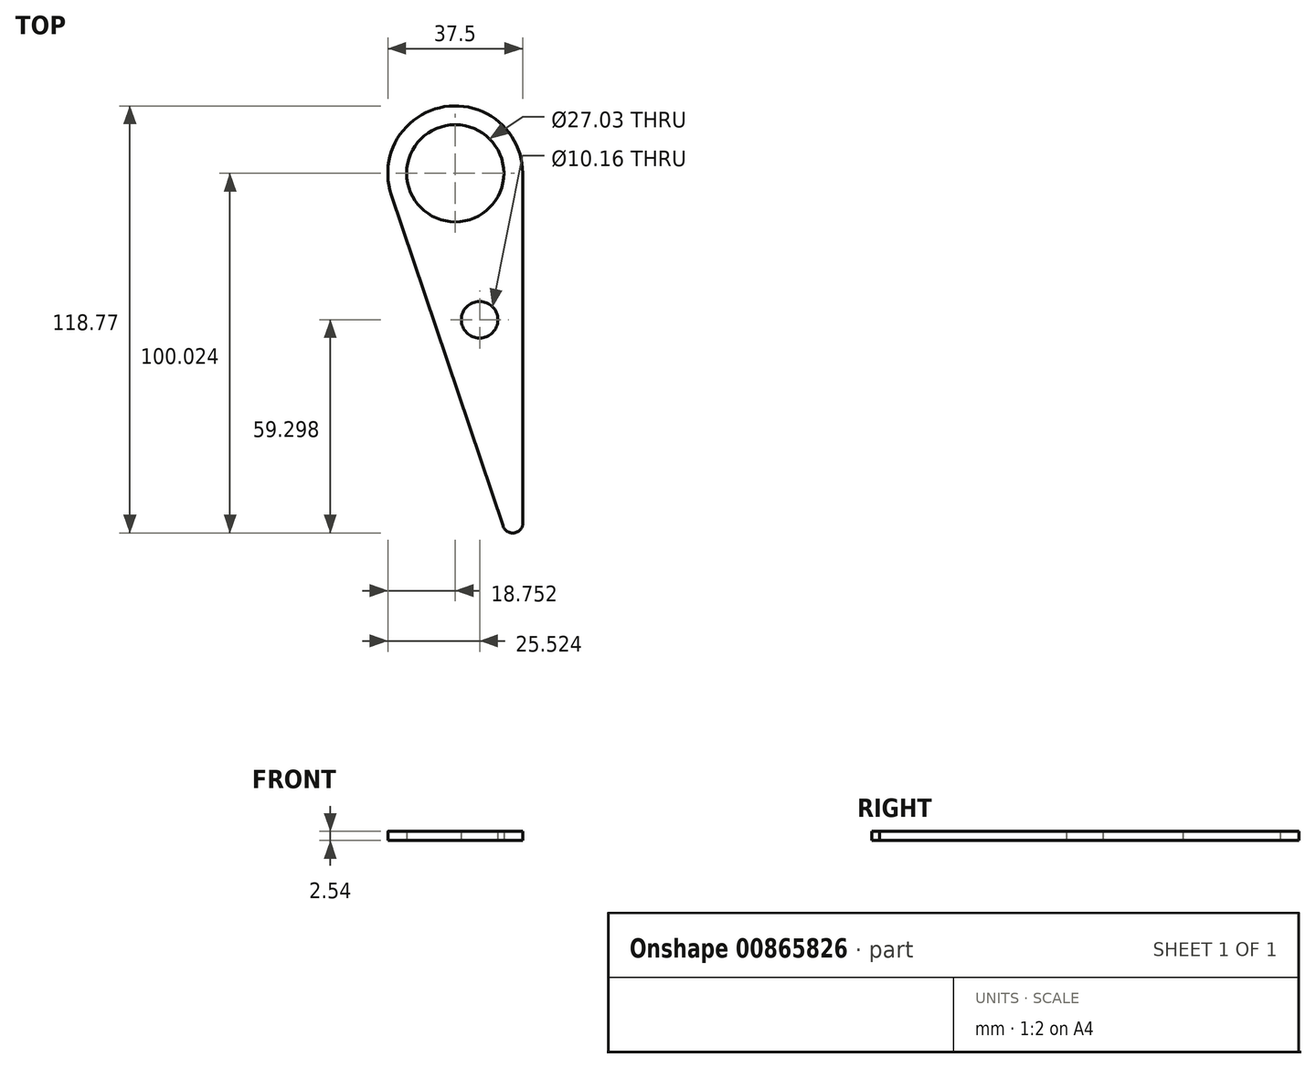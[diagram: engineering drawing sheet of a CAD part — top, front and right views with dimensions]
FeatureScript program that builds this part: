
annotation { "Feature Type Name" : "Feature", "Feature Type Description" : "" }
export const myFeature = defineFeature(function(context is Context, id is Id, definition is map)
    precondition{}
    {
        {
            var Q0;
            Q0=qCreatedBy(makeId("Top.planeOp"),FACE);
            var sketch = newSketch(context, id + "F0", { "sketchPlane" : qUnion([Q0])});
            skCircle(sketch, "E0", {"center": v(-25.2, 42.77) * mm, "radius": 13.52 * mm});
            skCircle(sketch, "E1", {"center": v(-25.2, 42.77) * mm, "radius": 18.75 * mm});
            skLineSegment(sketch, "E2", {"start": v(-6.46, 42.77) * mm, "end": v(-6.46, -55.07) * mm});
            skLineSegment(sketch, "E3", {"start": v(-42.97, 36.79) * mm, "end": v(-11.93, -55.3) * mm});
            skArc(sketch, "E4", {"start": v(-11.93, -55.3) * mm, "mid": v(-9.1, -57.24) * mm, "end": v(-6.46, -55.07) * mm});
            skSolve(sketch);
        }
        {
            var Q0;
            Q0=makeQuery(id+"F0.imprint","IMPRINT",FACE,{"disambiguationData":[TD([[makeQuery(id+"F0.imprint","IMPRINT",EDGE,{"derivedFrom":sQuery(id+"F0.wireOp",EDGE,"E0")}),-1.0]])]});
            var Q1;
            {var subQ0=sQuery(id+"F0.wireOp",EDGE,"E2");Q1=makeQuery(id+"F0.imprint","IMPRINT",FACE,{"disambiguationData":[TD([[makeQuery(id+"F0.imprint","IMPRINT",EDGE,{"derivedFrom":subQ0}),-1.0]])]});}
            extrude(context, id + "F1", {"entities" : qUnion([Q0, Q1]), "depth" : 2.54 * mm, "offsetDistance" : 25.4 * mm});
        }
        {
            var Q0;
            Q0=makeQuery(id+"F1.opExtrude","CAP_FACE",FACE,{"disambiguationData":[OSD([sQuery(id+"F0.wireOp",EDGE,"E0"),sQuery(id+"F0.wireOp",EDGE,"E1"),sQuery(id+"F0.wireOp",EDGE,"E2"),sQuery(id+"F0.wireOp",EDGE,"E3"),sQuery(id+"F0.wireOp",EDGE,"E4")])],"isStart":false});
            var sketch = newSketch(context, id + "F2", { "sketchPlane" : qUnion([Q0])});
            skCircle(sketch, "E5", {"center": v(-18.44, 2.05) * mm, "radius": 5.08 * mm});
            skSolve(sketch);
        }
        {
            var Q0;
            Q0 = qSketchRegion(id + "F2", true);
            extrude(context, id + "F3", {"entities" : qUnion([Q0]), "operationType" : NewBodyOperationType.REMOVE, "oppositeDirection" : true, "depth" : 12.2 * mm, "offsetDistance" : 25.4 * mm});
        }
    });
